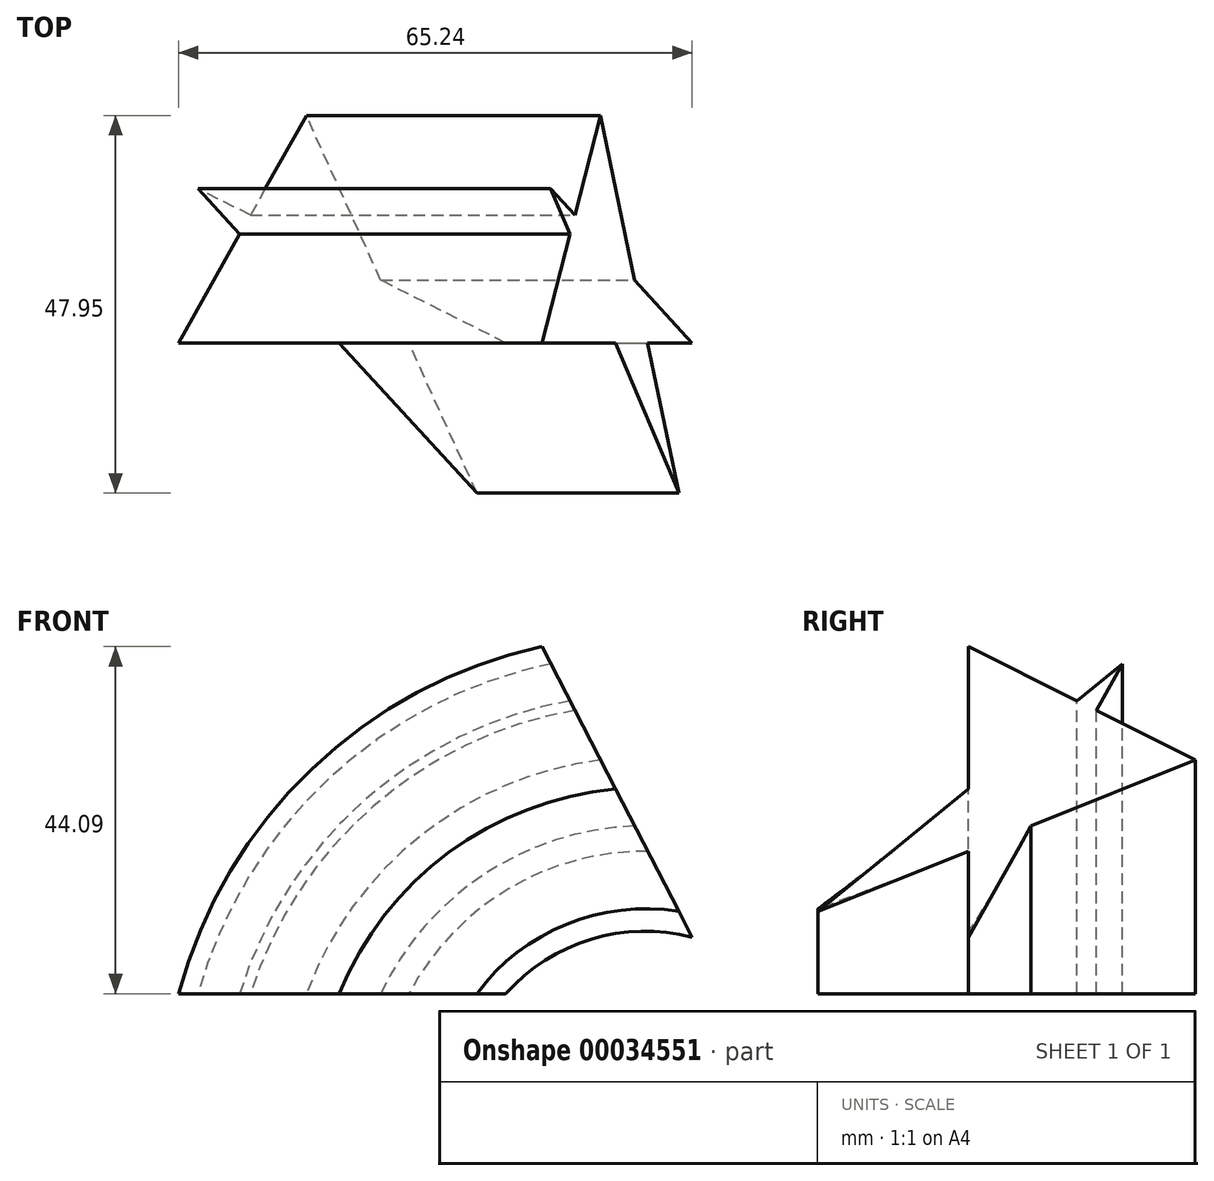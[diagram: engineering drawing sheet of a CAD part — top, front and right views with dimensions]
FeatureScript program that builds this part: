
annotation { "Feature Type Name" : "Feature", "Feature Type Description" : "" }
export const myFeature = defineFeature(function(context is Context, id is Id, definition is map)
    precondition{}
    {
        {
            var Q0;
            Q0=qCreatedBy(makeId("Top.planeOp"),FACE);
            var sketch = newSketch(context, id + "F0", { "sketchPlane" : qUnion([Q0])});
            skLineSegment(sketch, "E0", {"start": v(-20.94, 12.42) * mm, "end": v(-15.65, 6.65) * mm});
            skLineSegment(sketch, "E1", {"start": v(14.47, -26.23) * mm, "end": v(5.86, -7.14) * mm});
            skLineSegment(sketch, "E2", {"start": v(-7.17, 21.72) * mm, "end": v(-14.28, 9.09) * mm});
            skLineSegment(sketch, "E3", {"start": v(-23.41, -7.14) * mm, "end": v(-3.02, -7.14) * mm});
            skLineSegment(sketch, "E4", {"start": v(18.15, -7.14) * mm, "end": v(2.27, 0.8) * mm});
            skLineSegment(sketch, "E5.trimOffspring", {"start": v(-14.28, 9.09) * mm, "end": v(-20.94, 12.42) * mm});
            skLineSegment(sketch, "E6.trimOffspring", {"start": v(-3.02, -7.14) * mm, "end": v(14.47, -26.23) * mm});
            skLineSegment(sketch, "E7.trimOffspring", {"start": v(-15.65, 6.65) * mm, "end": v(-23.41, -7.14) * mm});
            skLineSegment(sketch, "E8.trimOffspring", {"start": v(5.86, -7.14) * mm, "end": v(18.15, -7.14) * mm});
            skLineSegment(sketch, "E9.trimOffspring", {"start": v(2.27, 0.8) * mm, "end": v(-7.17, 21.72) * mm});
            skSolve(sketch);
        }
        {
            var Q0;
            Q0=qCreatedBy(makeId("Front.planeOp"),FACE);
            var sketch = newSketch(context, id + "F1", { "sketchPlane" : qUnion([Q0])});
            skArc(sketch, "E10", {"start": v(26.84, 36.14) * mm, "mid": v(1.13, 23.86) * mm, "end": v(-14.45, 0) * mm});
            skSolve(sketch);
        }
        {
            var Q0;
            Q0=makeQuery(id+"F0.imprint","IMPRINT",FACE,{"disambiguationData":[TD([[makeQuery(id+"F0.imprint","IMPRINT",EDGE,{"derivedFrom":sQuery(id+"F0.wireOp",EDGE,"E0")}),1.0]])]});
            var Q1;
            Q1=sQuery(id+"F1.wireOp",EDGE,"E10");
            sweep(context, id + "F2", {"profiles" : qUnion([Q0]), "path" : qUnion([Q1])});
        }
    });
